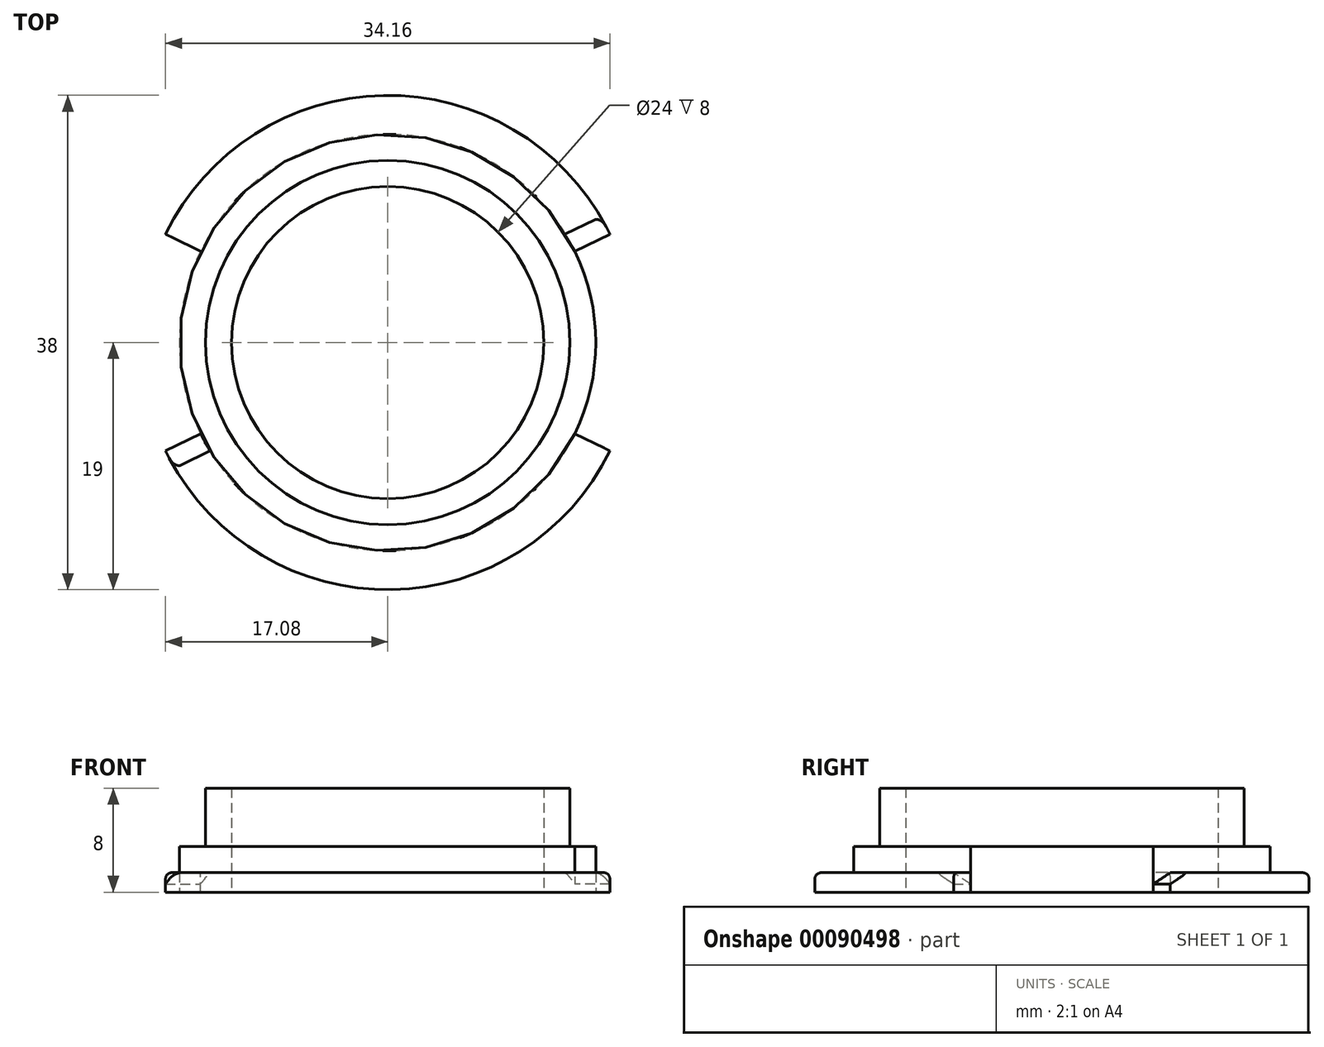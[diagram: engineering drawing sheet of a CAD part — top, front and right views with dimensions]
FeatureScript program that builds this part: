
annotation { "Feature Type Name" : "Feature", "Feature Type Description" : "" }
export const myFeature = defineFeature(function(context is Context, id is Id, definition is map)
    precondition{}
    {
        {
            var Q0;
            Q0=qCreatedBy(makeId("Top.planeOp"),FACE);
            var sketch = newSketch(context, id + "F0", { "sketchPlane" : qUnion([Q0])});
            skCircle(sketch, "E0", {"center": v(0, 0) * mm, "radius": 12 * mm});
            skCircle(sketch, "E1", {"center": v(0, 0) * mm, "radius": 14 * mm});
            skCircle(sketch, "E2", {"center": v(0, 0) * mm, "radius": 16 * mm});
            skCircle(sketch, "E3", {"center": v(0, 0) * mm, "radius": 19 * mm});
            skSolve(sketch);
        }
        {
            var Q0;
            Q0=makeQuery(id+"F0.imprint","IMPRINT",FACE,{"disambiguationData":[TD([[makeQuery(id+"F0.imprint","IMPRINT",EDGE,{"derivedFrom":sQuery(id+"F0.wireOp",EDGE,"E0")}),-1.0]])]});
            extrude(context, id + "F1", {"entities" : qUnion([Q0]), "depth" : 8 * mm});
        }
        {
            var Q0;
            Q0=makeQuery(id+"F0.imprint","IMPRINT",FACE,{"disambiguationData":[TD([[makeQuery(id+"F0.imprint","IMPRINT",EDGE,{"derivedFrom":sQuery(id+"F0.wireOp",EDGE,"E1")}),-1.0]])]});
            extrude(context, id + "F2", {"entities" : qUnion([Q0]), "operationType" : NewBodyOperationType.ADD, "depth" : 3.5 * mm});
        }
        {
            var Q0;
            Q0=makeQuery(id+"F0.imprint","IMPRINT",FACE,{"disambiguationData":[TD([[makeQuery(id+"F0.imprint","IMPRINT",EDGE,{"derivedFrom":sQuery(id+"F0.wireOp",EDGE,"E2")}),-1.0]])]});
            extrude(context, id + "F3", {"entities" : qUnion([Q0]), "operationType" : NewBodyOperationType.ADD, "depth" : 1.5 * mm});
        }
        {
            var Q0;
            Q0=qCreatedBy(makeId("Front.planeOp"),FACE);
            var sketch = newSketch(context, id + "F4", { "sketchPlane" : qUnion([Q0])});
            skLineSegment(sketch, "E4", {"start": v(0, -2.57) * mm, "end": v(0, 3.37) * mm});
            skSolve(sketch);
        }
        {
            var Q0;
            Q0=qCreatedBy(makeId("Front.planeOp"),FACE);
            var sketch = newSketch(context, id + "F5", { "sketchPlane" : qUnion([Q0])});
            skLineSegment(sketch, "E5.bottom", {"start": v(-19.79, 0) * mm, "end": v(-16, 0) * mm});
            skLineSegment(sketch, "E5.top", {"start": v(-19.79, 3.5) * mm, "end": v(-16, 3.5) * mm});
            skLineSegment(sketch, "E5.left", {"start": v(-19.79, 0) * mm, "end": v(-19.79, 3.5) * mm});
            skLineSegment(sketch, "E5.right", {"start": v(-16, 0) * mm, "end": v(-16, 3.5) * mm});
            skSolve(sketch);
        }
        {
            var Q0;
            Q0=makeQuery(id+"F5.imprint","IMPRINT",FACE,{"disambiguationData":[TD([[makeQuery(id+"F5.imprint","IMPRINT",EDGE,{"derivedFrom":sQuery(id+"F5.wireOp",EDGE,"E5.bottom")}),1.0]])]});
            var Q1;
            Q1=sQuery(id+"F4.wireOp",EDGE,"E4");
            revolve(context, id + "F6", {"operationType" : NewBodyOperationType.REMOVE, "entities" : qUnion([Q0]), "axis" : qUnion([Q1]), "revolveType" : RevolveType.SYMMETRIC, "angle" : 52 * degree});
        }
        {
            var Q0;
            Q0=qCreatedBy(makeId("Front.planeOp"),FACE);
            var sketch = newSketch(context, id + "F7", { "sketchPlane" : qUnion([Q0])});
            skLineSegment(sketch, "E6.bottom", {"start": v(15.99, 3.52) * mm, "end": v(21.2, 3.52) * mm});
            skLineSegment(sketch, "E6.top", {"start": v(15.99, -0.48) * mm, "end": v(21.2, -0.48) * mm});
            skLineSegment(sketch, "E6.left", {"start": v(15.99, 3.52) * mm, "end": v(15.99, -0.48) * mm});
            skLineSegment(sketch, "E6.right", {"start": v(21.2, 3.52) * mm, "end": v(21.2, -0.48) * mm});
            skSolve(sketch);
        }
        {
            var Q0;
            Q0=makeQuery(id+"F7.imprint","IMPRINT",FACE,{"disambiguationData":[TD([[makeQuery(id+"F7.imprint","IMPRINT",EDGE,{"derivedFrom":sQuery(id+"F7.wireOp",EDGE,"E6.bottom")}),-1.0]])]});
            var Q1;
            Q1=sQuery(id+"F4.wireOp",EDGE,"E4");
            revolve(context, id + "F8", {"operationType" : NewBodyOperationType.REMOVE, "entities" : qUnion([Q0]), "axis" : qUnion([Q1]), "revolveType" : RevolveType.SYMMETRIC, "angle" : 52 * degree});
        }
        {
            var Q0;
            Q0=makeQuery(id+"F6.boolean.opBoolean","INTERSECT",EDGE,{"derivedFrom":[makeQuery(id+"F3.opExtrude","CAP_FACE",FACE,{"disambiguationData":[OSD([sQuery(id+"F0.wireOp",EDGE,"E2"),sQuery(id+"F0.wireOp",EDGE,"E3")])],"isStart":false}),makeQuery(id+"F6.opRevolve","CAP_FACE",FACE,{"disambiguationData":[OSD([sQuery(id+"F5.wireOp",EDGE,"E5.bottom"),sQuery(id+"F5.wireOp",EDGE,"E5.top"),sQuery(id+"F5.wireOp",EDGE,"E5.left"),sQuery(id+"F5.wireOp",EDGE,"E5.right")])],"isStart":false})]});
            chamfer(context, id + "F9", {"entities" : qUnion([Q0]), "chamferType" : ChamferType.OFFSET_ANGLE, "width" : 1.5 * mm, "oppositeDirection" : true, "angle" : 30 * degree});
        }
        {
            var Q0;
            Q0=makeQuery(id+"F8.boolean.opBoolean","INTERSECT",EDGE,{"derivedFrom":[makeQuery(id+"F3.opExtrude","CAP_FACE",FACE,{"disambiguationData":[OSD([sQuery(id+"F0.wireOp",EDGE,"E2"),sQuery(id+"F0.wireOp",EDGE,"E3")])],"isStart":false}),makeQuery(id+"F8.opRevolve","CAP_FACE",FACE,{"disambiguationData":[OSD([sQuery(id+"F7.wireOp",EDGE,"E6.bottom"),sQuery(id+"F7.wireOp",EDGE,"E6.top"),sQuery(id+"F7.wireOp",EDGE,"E6.left"),sQuery(id+"F7.wireOp",EDGE,"E6.right")])],"isStart":false})]});
            chamfer(context, id + "F10", {"entities" : qUnion([Q0]), "chamferType" : ChamferType.OFFSET_ANGLE, "width" : 1.5 * mm, "oppositeDirection" : false, "angle" : 30 * degree});
        }
        {
            var Q0;
            {var subQ0=sQuery(id+"F0.wireOp",EDGE,"E3");Q0=makeQuery(id+"F8.boolean.opBoolean","SPLIT",EDGE,{"disambiguationData":[TD([makeQuery(id+"F6.boolean.opBoolean","COPY",FACE,{"derivedFrom":makeQuery(id+"F6.opRevolve","CAP_FACE",FACE,{"disambiguationData":[OSD([sQuery(id+"F5.wireOp",EDGE,"E5.bottom"),sQuery(id+"F5.wireOp",EDGE,"E5.top"),sQuery(id+"F5.wireOp",EDGE,"E5.left"),sQuery(id+"F5.wireOp",EDGE,"E5.right")])],"isStart":true})})])],"derivedFrom":makeQuery(id+"F3.opExtrude","CAP_EDGE",EDGE,{"disambiguationData":[OSD([subQ0])],"isStart":false})});}
            fillet(context, id + "F11", {"entities" : qUnion([Q0]), "radius" : 0.5 * mm, "allowEdgeOverflow" : false});
        }
        {
            var Q0;
            {var subQ0=sQuery(id+"F0.wireOp",EDGE,"E3");Q0=makeQuery(id+"F8.boolean.opBoolean","SPLIT",EDGE,{"disambiguationData":[TD([makeQuery(id+"F6.boolean.opBoolean","COPY",FACE,{"derivedFrom":makeQuery(id+"F6.opRevolve","CAP_FACE",FACE,{"disambiguationData":[OSD([sQuery(id+"F5.wireOp",EDGE,"E5.bottom"),sQuery(id+"F5.wireOp",EDGE,"E5.top"),sQuery(id+"F5.wireOp",EDGE,"E5.left"),sQuery(id+"F5.wireOp",EDGE,"E5.right")])],"isStart":false})})])],"derivedFrom":makeQuery(id+"F3.opExtrude","CAP_EDGE",EDGE,{"disambiguationData":[OSD([subQ0])],"isStart":false})});}
            fillet(context, id + "F12", {"entities" : qUnion([Q0]), "radius" : 0.5 * mm, "allowEdgeOverflow" : false});
        }
    });
